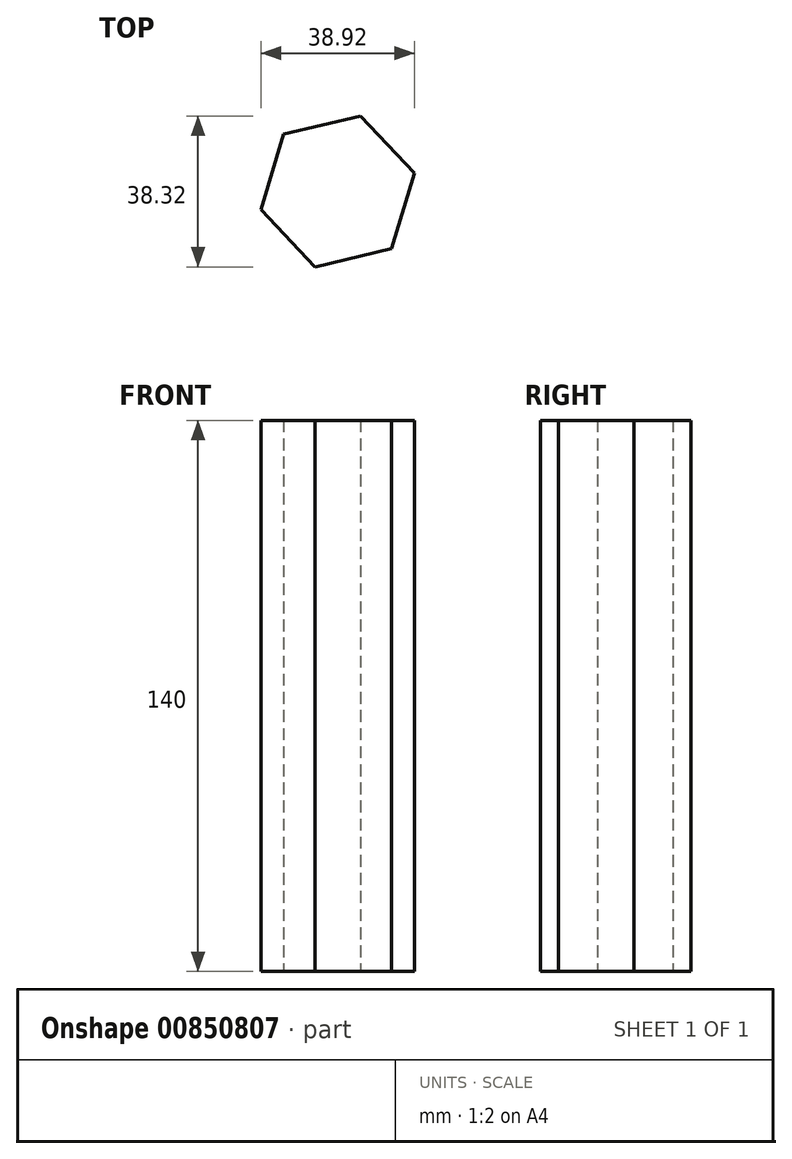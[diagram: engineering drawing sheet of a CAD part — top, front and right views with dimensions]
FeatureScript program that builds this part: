
annotation { "Feature Type Name" : "Feature", "Feature Type Description" : "" }
export const myFeature = defineFeature(function(context is Context, id is Id, definition is map)
    precondition{}
    {
        {
            var Q0;
            Q0=qCreatedBy(makeId("Top.planeOp"),FACE);
            var sketch = newSketch(context, id + "F0", { "sketchPlane" : qUnion([Q0])});
            skCircle(sketch, "E0.cCircle", {"center": v(0, 0) * mm, "radius": 17.32 * mm, "construction": true});
            skLineSegment(sketch, "E0.0", {"start": v(5.74, 19.16) * mm, "end": v(19.46, 4.61) * mm});
            skLineSegment(sketch, "E0.1", {"start": v(19.46, 4.61) * mm, "end": v(13.72, -14.55) * mm});
            skLineSegment(sketch, "E0.2", {"start": v(13.72, -14.55) * mm, "end": v(-5.74, -19.16) * mm});
            skLineSegment(sketch, "E0.3", {"start": v(-5.74, -19.16) * mm, "end": v(-19.46, -4.61) * mm});
            skLineSegment(sketch, "E0.4", {"start": v(-19.46, -4.61) * mm, "end": v(-13.72, 14.55) * mm});
            skLineSegment(sketch, "E0.5", {"start": v(-13.72, 14.55) * mm, "end": v(5.74, 19.16) * mm});
            skPoint(sketch, "E0.0.midPoint", {"position": v(12.6, 11.89) * mm});
            skSolve(sketch);
        }
        {
            var Q0;
            Q0=makeQuery(id+"F0.imprint","IMPRINT",FACE,{"disambiguationData":[TD([[makeQuery(id+"F0.imprint","IMPRINT",EDGE,{"derivedFrom":sQuery(id+"F0.wireOp",EDGE,"E0.0")}),-1.0]])]});
            extrude(context, id + "F1", {"entities" : qUnion([Q0]), "depth" : 140 * mm, "offsetDistance" : 25 * mm});
        }
    });
